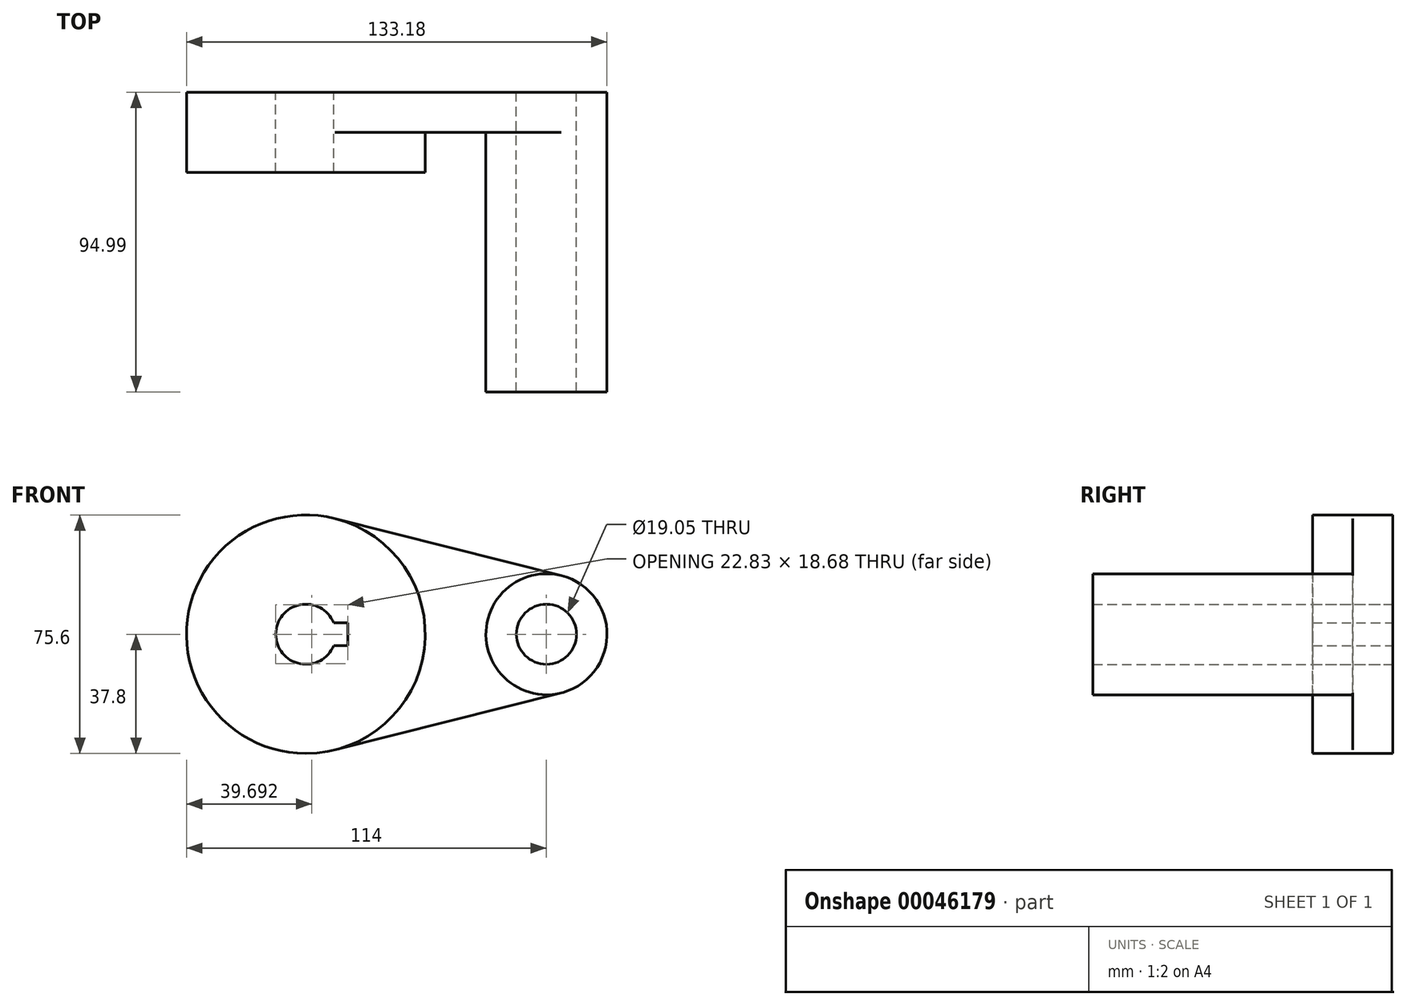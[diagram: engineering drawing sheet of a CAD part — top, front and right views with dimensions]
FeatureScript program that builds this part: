
annotation { "Feature Type Name" : "Feature", "Feature Type Description" : "" }
export const myFeature = defineFeature(function(context is Context, id is Id, definition is map)
    precondition{}
    {
        {
            var Q0;
            Q0=qCreatedBy(makeId("Front.planeOp"),FACE);
            var sketch = newSketch(context, id + "F0", { "sketchPlane" : qUnion([Q0])});
            skCircle(sketch, "E0", {"center": v(0, 0) * mm, "radius": 37.8 * mm});
            skCircle(sketch, "E1", {"center": v(76.2, 0) * mm, "radius": 19.18 * mm});
            skLineSegment(sketch, "E2", {"start": v(9.24, 36.65) * mm, "end": v(80.89, 18.6) * mm});
            skLineSegment(sketch, "E3", {"start": v(9.24, -36.65) * mm, "end": v(80.89, -18.6) * mm});
            skCircle(sketch, "E4", {"center": v(0, 0) * mm, "radius": 9.53 * mm});
            skCircle(sketch, "E5", {"center": v(76.2, 0) * mm, "radius": 9.53 * mm});
            skLineSegment(sketch, "E6.rect.bottom", {"start": v(13.3, -3.67) * mm, "end": v(-13.3, -3.67) * mm});
            skLineSegment(sketch, "E6.rect.top", {"start": v(13.3, 3.67) * mm, "end": v(-13.3, 3.67) * mm});
            skLineSegment(sketch, "E6.rect.left", {"start": v(13.3, -3.67) * mm, "end": v(13.3, 3.67) * mm});
            skLineSegment(sketch, "E6.rect.right", {"start": v(-13.3, -3.67) * mm, "end": v(-13.3, 3.67) * mm});
            skSolve(sketch);
        }
        {
            var Q0;
            {var subQ5=sQuery(id+"F0.wireOp",EDGE,"E6.rect.left");Q0=makeQuery(id+"F0.imprint","IMPRINT",FACE,{"disambiguationData":[TD([[makeQuery(id+"F0.imprint","IMPRINT",EDGE,{"derivedFrom":subQ5}),-1.0]])]});}
            var Q1;
            {var subQ0=sQuery(id+"F0.wireOp",EDGE,"E6.rect.right");Q1=makeQuery(id+"F0.imprint","IMPRINT",FACE,{"disambiguationData":[TD([[makeQuery(id+"F0.imprint","IMPRINT",EDGE,{"derivedFrom":subQ0}),-1.0]])]});}
            extrude(context, id + "F1", {"entities" : qUnion([Q0, Q1]), "depth" : 25.4 * mm});
        }
        {
            var Q0;
            {var subQ1=sQuery(id+"F0.wireOp",EDGE,"E2");Q0=makeQuery(id+"F0.imprint","IMPRINT",FACE,{"disambiguationData":[TD([[makeQuery(id+"F0.imprint","IMPRINT",EDGE,{"derivedFrom":subQ1}),-1.0]])]});}
            extrude(context, id + "F2", {"entities" : qUnion([Q0]), "operationType" : NewBodyOperationType.ADD, "depth" : 12.7 * mm});
        }
        {
            var Q0;
            Q0=makeQuery(id+"F0.imprint","IMPRINT",FACE,{"disambiguationData":[TD([[makeQuery(id+"F0.imprint","IMPRINT",EDGE,{"derivedFrom":sQuery(id+"F0.wireOp",EDGE,"E5")}),-1.0]])]});
            extrude(context, id + "F3", {"entities" : qUnion([Q0]), "operationType" : NewBodyOperationType.ADD, "depth" : 94.99 * mm});
        }
    });
